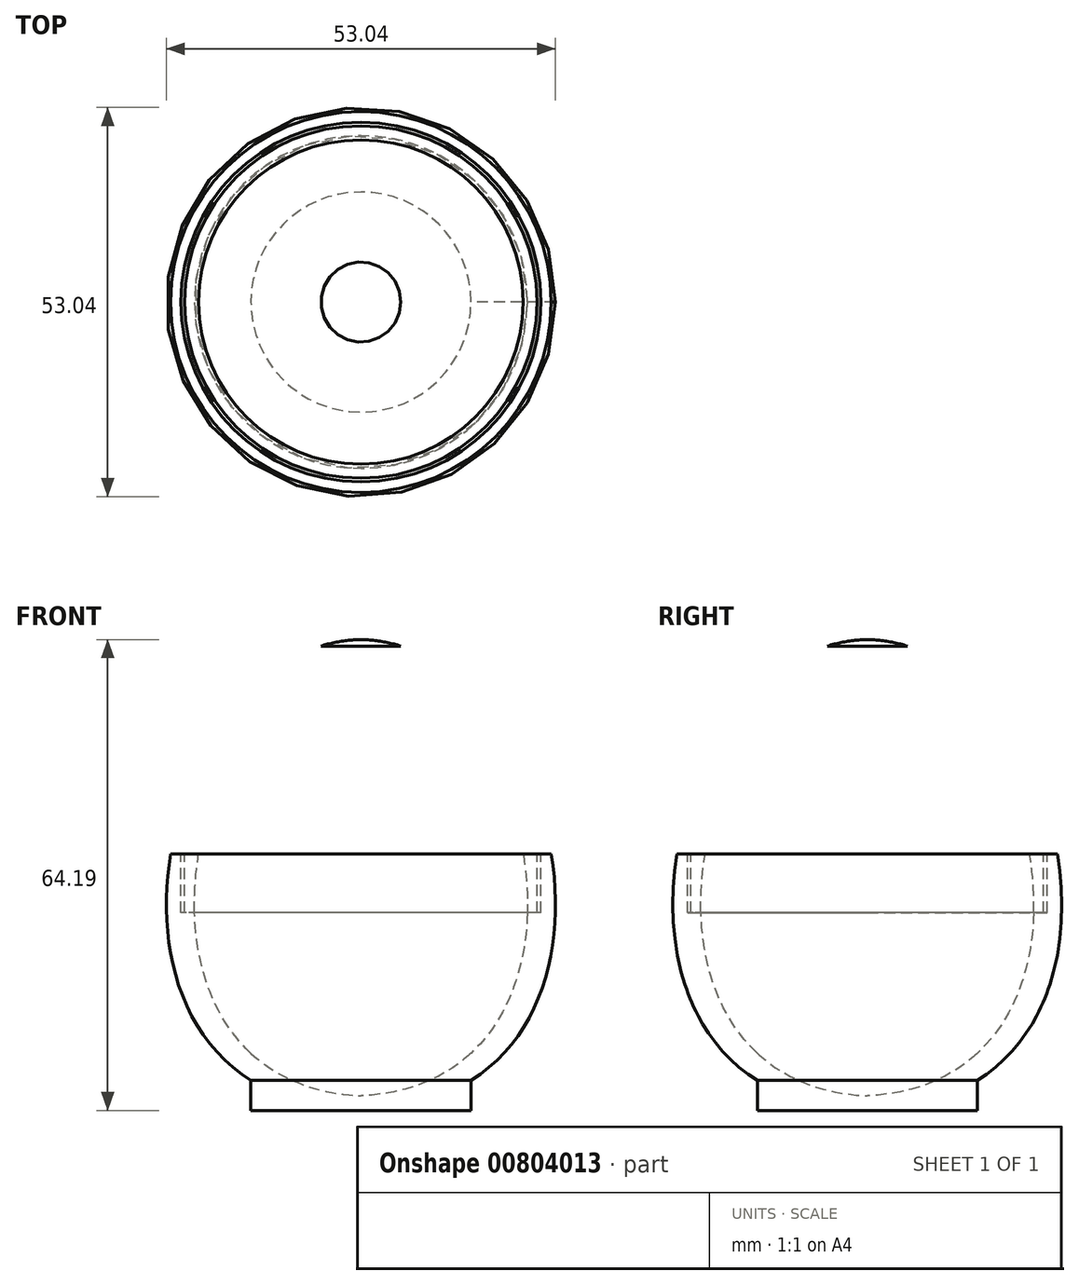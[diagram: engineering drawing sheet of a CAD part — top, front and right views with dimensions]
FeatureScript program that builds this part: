
annotation { "Feature Type Name" : "Feature", "Feature Type Description" : "" }
export const myFeature = defineFeature(function(context is Context, id is Id, definition is map)
    precondition{}
    {
        {
            var Q0;
            Q0=qCreatedBy(makeId("Front.planeOp"),FACE);
            var sketch = newSketch(context, id + "F0", { "sketchPlane" : qUnion([Q0])});
            skLineSegment(sketch, "E0", {"start": v(-24.03, 32) * mm, "end": v(24.03, -32) * mm, "construction": true});
            skLineSegment(sketch, "E1", {"start": v(-24.03, -32) * mm, "end": v(24.03, 32) * mm, "construction": true});
            skPoint(sketch, "E2", {"position": v(0, 0) * mm});
            skFitSpline(sketch, "E3", {"points": [v(0, 30.88) * mm, v(0, -29.31) * mm], "startDerivative": vector(-77.7, -13.18) * mm, "endDerivative": vector(103, -4.83) * mm});
            skLineSegment(sketch, "E4", {"start": v(0, 32) * mm, "end": v(0, -32) * mm});
            skLineSegment(sketch, "E5", {"start": v(0, 30.88) * mm, "end": v(0, 32.88) * mm});
            skLineSegment(sketch, "E6", {"start": v(0, -29.31) * mm, "end": v(0, -31.31) * mm});
            skFitSpline(sketch, "E7", {"points": [v(0, 32.88) * mm, v(0, -31.31) * mm], "startDerivative": vector(-86.36, -1.77) * mm, "endDerivative": vector(124.13, -2.62) * mm});
            skLineSegment(sketch, "E8", {"start": v(-25.95, 3.65) * mm, "end": v(-22.11, 3.65) * mm});
            skLineSegment(sketch, "E9", {"start": v(-24.03, 3.65) * mm, "end": v(-24.03, -4.35) * mm});
            skLineSegment(sketch, "E10", {"start": v(-24.03, -4.35) * mm, "end": v(-22.68, -4.35) * mm});
            skLineSegment(sketch, "E11", {"start": v(-24.03, 32) * mm, "end": v(24.03, 32) * mm});
            skLineSegment(sketch, "E12.bottom", {"start": v(0, -31.31) * mm, "end": v(-15, -31.31) * mm});
            skLineSegment(sketch, "E12.top", {"start": v(0, -22.43) * mm, "end": v(-15, -22.43) * mm});
            skLineSegment(sketch, "E12.left", {"start": v(0, -31.31) * mm, "end": v(0, -22.43) * mm});
            skLineSegment(sketch, "E12.right", {"start": v(-15, -31.31) * mm, "end": v(-15, -22.43) * mm});
            skLineSegment(sketch, "E13.bottom", {"start": v(-24.03, 3.65) * mm, "end": v(-24.53, 3.65) * mm});
            skLineSegment(sketch, "E13.top", {"start": v(-24.03, -4.35) * mm, "end": v(-24.53, -4.35) * mm});
            skLineSegment(sketch, "E13.right", {"start": v(-24.53, 3.65) * mm, "end": v(-24.53, -4.35) * mm});
            skSolve(sketch);
        }
        {
            var Q0;
            {var subQ0=sQuery(id+"F0.wireOp",EDGE,"E7");var subQ1=sQuery(id+"F0.wireOp",EDGE,"E5");var subQ2=makeQuery(id+"F0.imprint","INTERSECT",VERTEX,{"derivedFrom":[subQ1,subQ0]});Q0=makeQuery(id+"F0.imprint","IMPRINT",FACE,{"disambiguationData":[TD([[makeQuery(id+"F0.imprint","IMPRINT",EDGE,{"disambiguationData":[TD([[subQ2,1.0]])],"derivedFrom":subQ1}),1.0]])]});}
            var Q1;
            {var subQ3=sQuery(id+"F0.wireOp",EDGE,"E13.bottom");Q1=makeQuery(id+"F0.imprint","IMPRINT",FACE,{"disambiguationData":[TD([[makeQuery(id+"F0.imprint","IMPRINT",EDGE,{"derivedFrom":subQ3}),-1.0]])]});}
            var Q2;
            {var subQ3=sQuery(id+"F0.wireOp",EDGE,"E10");Q2=makeQuery(id+"F0.imprint","IMPRINT",FACE,{"disambiguationData":[TD([[makeQuery(id+"F0.imprint","IMPRINT",EDGE,{"derivedFrom":subQ3}),1.0]])]});}
            var Q3;
            Q3=sQuery(id+"F0.wireOp",EDGE,"E4");
            revolve(context, id + "F1", {"surfaceOperationType" : NewSurfaceOperationType.NEW, "entities" : qUnion([Q0, Q1, Q2]), "axis" : qUnion([Q3]), "revolveType" : RevolveType.FULL});
        }
        {
            var Q0;
            {var subQ0=sQuery(id+"F0.wireOp",EDGE,"E12.bottom");Q0=makeQuery(id+"F0.imprint","IMPRINT",FACE,{"disambiguationData":[TD([[makeQuery(id+"F0.imprint","IMPRINT",EDGE,{"derivedFrom":subQ0}),-1.0]])]});}
            var Q1;
            {var subQ0=sQuery(id+"F0.wireOp",EDGE,"E12.left");var subQ1=sQuery(id+"F0.wireOp",EDGE,"E3");var subQ2=makeQuery(id+"F0.imprint","INTERSECT",VERTEX,{"derivedFrom":[subQ1,subQ0]});Q1=makeQuery(id+"F0.imprint","IMPRINT",FACE,{"disambiguationData":[TD([[makeQuery(id+"F0.imprint","IMPRINT",EDGE,{"disambiguationData":[TD([[subQ2,1.0]])],"derivedFrom":subQ1}),-1.0]])]});}
            var Q2;
            {var subQ0=sQuery(id+"F0.wireOp",EDGE,"E10");Q2=makeQuery(id+"F0.imprint","IMPRINT",FACE,{"disambiguationData":[TD([[makeQuery(id+"F0.imprint","IMPRINT",EDGE,{"derivedFrom":subQ0}),-1.0]])]});}
            var Q3;
            Q3=sQuery(id+"F0.wireOp",EDGE,"E4");
            revolve(context, id + "F2", {"surfaceOperationType" : NewSurfaceOperationType.NEW, "entities" : qUnion([Q0, Q1, Q2]), "axis" : qUnion([Q3]), "revolveType" : RevolveType.FULL});
        }
    });
